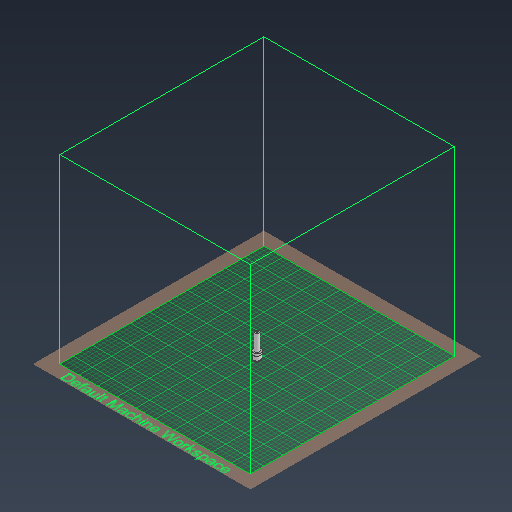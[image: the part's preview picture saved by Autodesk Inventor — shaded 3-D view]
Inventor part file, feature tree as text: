
AUTODESK INVENTOR PART (.ipt)
format: ipt  version: 2021 (Build 250183000, 183)  size: 280,576 bytes
history: native  units: mm
features: extrude x6, sketch x6
ambient origin geometry x8: Origin, YZ Plane, XZ Plane, XY Plane, X Axis, Y Axis, Z Axis, Center Point
bodies: Volumenkörper1 (feature_tree)
feature tree (12):
  extrude  "Extrusion1"  Depth=9.5mm
  extrude  "Extrusion2"  Depth=3.0mm
  extrude  "Extrusion5"  Depth=10.0mm
  extrude  "Extrusion6"  Depth=5.0mm
  extrude  "Extrusion7"  Depth=5.0mm
  extrude  "Extrusion8"  Depth=5.0mm
  sketch  "Skizze1"  dims[d0=9.5mm d1=9.5mm]
  sketch  "Skizze2"  dims[d2=3.0mm d3=0.0mm d4=14.8mm]
  sketch  "Skizze5"  dims[d5=10.0mm d6=0.0mm d13=4.0mm]
  sketch  "Skizze6"  dims[d14=5.0mm d15=0.0mm d16=17.0mm]
  sketch  "Skizze7"  dims[d17=5.0mm d18=0.0mm d19=9.8mm]
  sketch  "Skizze8"  dims[d20=36.0mm d21=0.0mm d22=4.0mm d23=5.0mm d24=0.0mm]
